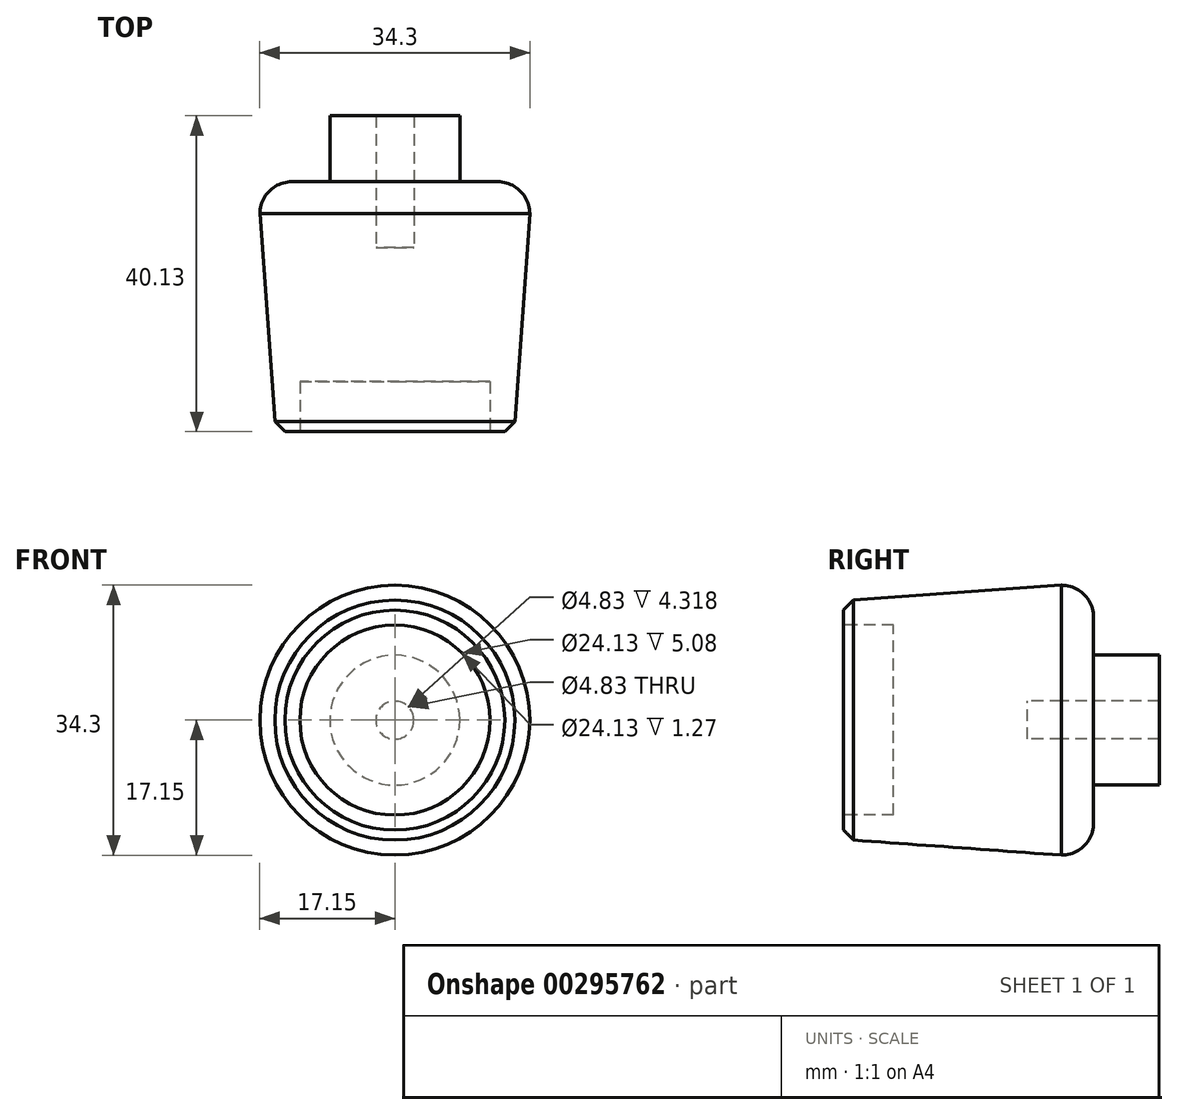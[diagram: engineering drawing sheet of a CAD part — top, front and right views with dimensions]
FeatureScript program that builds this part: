
annotation { "Feature Type Name" : "Feature", "Feature Type Description" : "" }
export const myFeature = defineFeature(function(context is Context, id is Id, definition is map)
    precondition{}
    {
        {
            var Q0;
            Q0=qCreatedBy(makeId("Front.planeOp"),FACE);
            var sketch = newSketch(context, id + "F0", { "sketchPlane" : qUnion([Q0])});
            skCircle(sketch, "E0", {"center": v(0, 0) * mm, "radius": 17.15 * mm});
            skSolve(sketch);
        }
        {
            var Q0;
            Q0=qCreatedBy(makeId("Front.planeOp"),FACE);
            var sketch = newSketch(context, id + "F1", { "sketchPlane" : qUnion([Q0])});
            skCircle(sketch, "E1", {"center": v(0, 0) * mm, "radius": 8.26 * mm});
            skSolve(sketch);
        }
        {
            var Q0;
            Q0=qCreatedBy(makeId("Front.planeOp"),FACE);
            var sketch = newSketch(context, id + "F2", { "sketchPlane" : qUnion([Q0])});
            skCircle(sketch, "E2", {"center": v(0, 0) * mm, "radius": 2.41 * mm});
            skSolve(sketch);
        }
        {
            var Q0;
            Q0=qCreatedBy(makeId("Front.planeOp"),FACE);
            cPlane(context, id + "F3", {"entities" : qUnion([Q0]), "cplaneType" : CPlaneType.OFFSET, "offset" : 31.75 * mm, "width" : 152.4 * mm, "height" : 152.4 * mm});
        }
        {
            var Q0;
            Q0=qCreatedBy(id+"F3.planeOp",FACE);
            var sketch = newSketch(context, id + "F4", { "sketchPlane" : qUnion([Q0])});
            skCircle(sketch, "E3", {"center": v(0, 0) * mm, "radius": 12.07 * mm});
            skSolve(sketch);
        }
        {
            var Q0;
            Q0=qCreatedBy(id+"F3.planeOp",FACE);
            var sketch = newSketch(context, id + "F5", { "sketchPlane" : qUnion([Q0])});
            skCircle(sketch, "E4", {"center": v(0, 0) * mm, "radius": 15.24 * mm});
            skSolve(sketch);
        }
        {
            var Q0;
            Q0=makeQuery(id+"F0.imprint","IMPRINT",FACE,{"disambiguationData":[TD([[makeQuery(id+"F0.imprint","IMPRINT",EDGE,{"derivedFrom":sQuery(id+"F0.wireOp",EDGE,"E0")}),1.0]])]});
            extrude(context, id + "F6", {"entities" : qUnion([Q0]), "depth" : 4.06 * mm});
        }
        {
            var Q0;
            Q0=makeQuery(id+"F6.opExtrude","CAP_FACE",FACE,{"disambiguationData":[OSD([sQuery(id+"F0.wireOp",EDGE,"E0")])],"isStart":true});
            fillet(context, id + "F7", {"entities" : qUnion([Q0]), "radius" : 4.06 * mm, "tangentPropagation" : true, "allowEdgeOverflow" : false});
        }
        {
            var Q0;
            Q0=makeQuery(id+"F5.imprint","IMPRINT",FACE,{"disambiguationData":[TD([[makeQuery(id+"F5.imprint","IMPRINT",EDGE,{"derivedFrom":sQuery(id+"F5.wireOp",EDGE,"E4")}),1.0]])]});
            extrude(context, id + "F8", {"entities" : qUnion([Q0]), "oppositeDirection" : true, "depth" : 1.27 * mm});
        }
        {
            var Q0;
            Q0=makeQuery(id+"F8.opExtrude","CAP_FACE",FACE,{"disambiguationData":[OSD([sQuery(id+"F5.wireOp",EDGE,"E4")])],"isStart":true});
            chamfer(context, id + "F9", {"entities" : qUnion([Q0]), "width" : 1.27 * mm, "tangentPropagation" : true});
        }
        {
            var Q0;
            Q0=makeQuery(id+"F6.opExtrude","CAP_FACE",FACE,{"disambiguationData":[OSD([sQuery(id+"F0.wireOp",EDGE,"E0")])],"isStart":false});
            var Q1;
            Q1=makeQuery(id+"F8.opExtrude","CAP_FACE",FACE,{"disambiguationData":[OSD([sQuery(id+"F5.wireOp",EDGE,"E4")])],"isStart":false});
            loft(context, id + "F10", {"sheetProfilesArray" : [{ "sheetProfileEntities" : qUnion([Q0]) }, { "sheetProfileEntities" : qUnion([Q1]) }]});
        }
        {
            var Q0;
            Q0=makeQuery(id+"F1.imprint","IMPRINT",FACE,{"disambiguationData":[TD([[makeQuery(id+"F1.imprint","IMPRINT",EDGE,{"derivedFrom":sQuery(id+"F1.wireOp",EDGE,"E1")}),1.0]])]});
            extrude(context, id + "F11", {"entities" : qUnion([Q0]), "operationType" : NewBodyOperationType.ADD, "oppositeDirection" : true, "depth" : 8.38 * mm});
        }
        {
            var Q0;
            Q0=makeQuery(id+"F2.imprint","IMPRINT",FACE,{"disambiguationData":[TD([[makeQuery(id+"F2.imprint","IMPRINT",EDGE,{"derivedFrom":sQuery(id+"F2.wireOp",EDGE,"E2")}),1.0]])]});
            extrude(context, id + "F12", {"entities" : qUnion([Q0]), "operationType" : NewBodyOperationType.REMOVE, "oppositeDirection" : true, "depth" : 8.38 * mm, "hasSecondDirection" : true, "secondDirectionOppositeDirection" : false, "secondDirectionDepth" : 8.38 * mm});
        }
        {
            var Q0;
            Q0=makeQuery(id+"F4.imprint","IMPRINT",FACE,{"disambiguationData":[TD([[makeQuery(id+"F4.imprint","IMPRINT",EDGE,{"derivedFrom":sQuery(id+"F4.wireOp",EDGE,"E3")}),1.0]])]});
            extrude(context, id + "F13", {"entities" : qUnion([Q0]), "operationType" : NewBodyOperationType.REMOVE, "oppositeDirection" : true, "depth" : 6.35 * mm});
        }
    });
